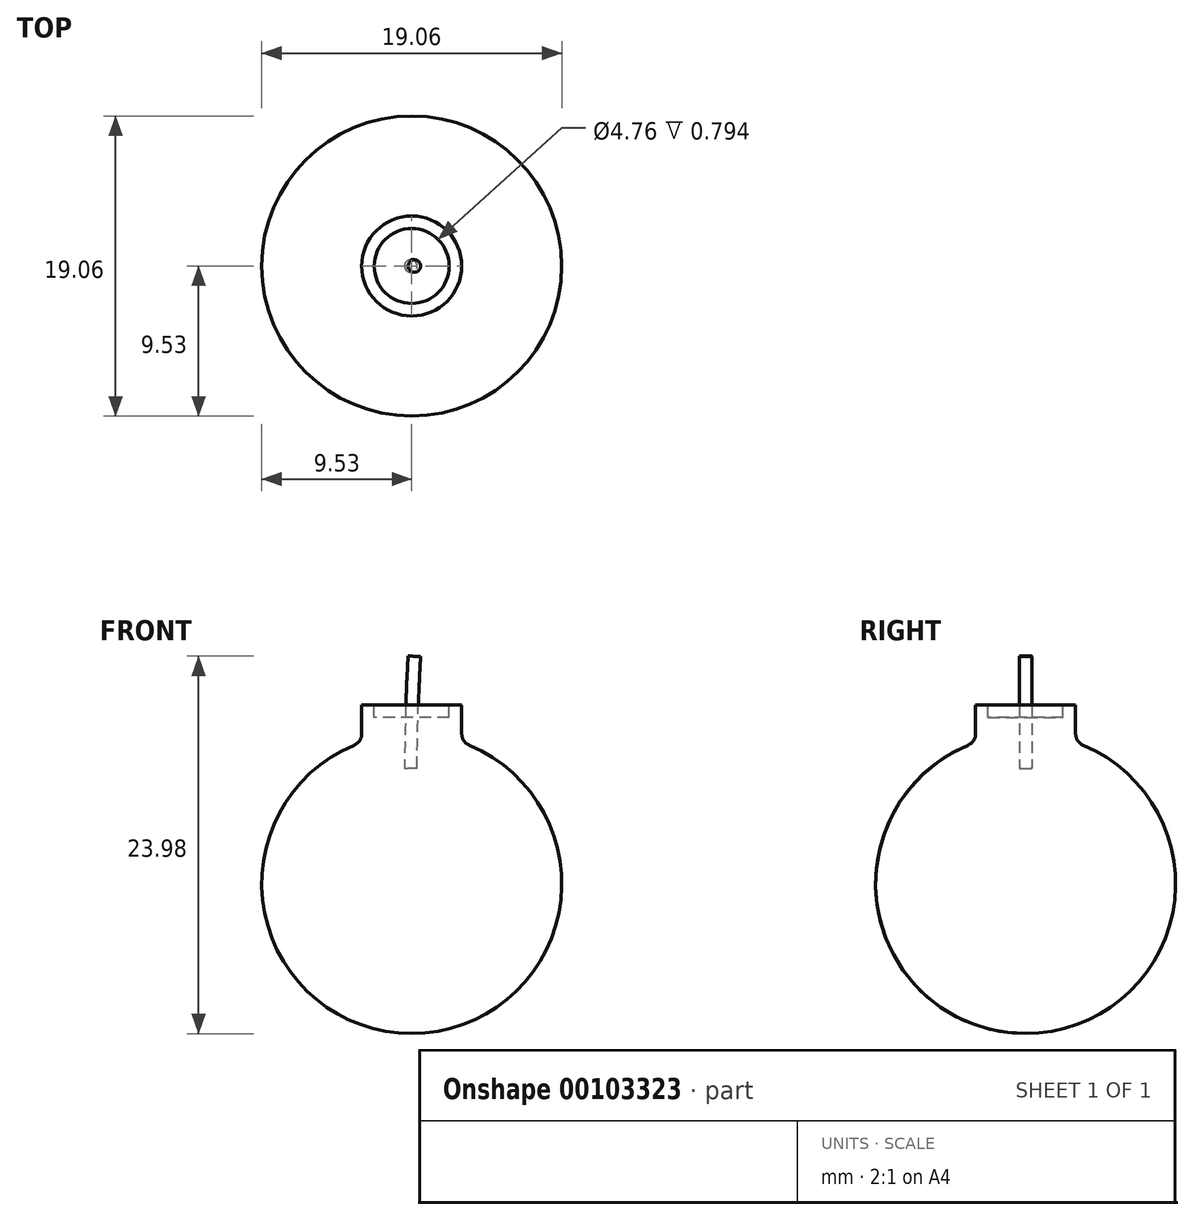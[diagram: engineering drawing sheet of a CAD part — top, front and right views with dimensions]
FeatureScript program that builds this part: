
annotation { "Feature Type Name" : "Feature", "Feature Type Description" : "" }
export const myFeature = defineFeature(function(context is Context, id is Id, definition is map)
    precondition{}
    {
        {
            var Q0;
            Q0=qCreatedBy(makeId("Right.planeOp"),FACE);
            var sketch = newSketch(context, id + "F0", { "sketchPlane" : qUnion([Q0])});
            skArc(sketch, "E0", {"start": v(0, 38.1) * mm, "mid": v(-38.1, 0) * mm, "end": v(0, -38.1) * mm});
            skLineSegment(sketch, "E1", {"start": v(0, 64.9) * mm, "end": v(0, -66.83) * mm});
            skSolve(sketch);
        }
        {
            var Q0;
            {var subQ0=sQuery(id+"F0.wireOp",EDGE,"E0");Q0=makeQuery(id+"F0.imprint","IMPRINT",FACE,{"disambiguationData":[TD([[makeQuery(id+"F0.imprint","IMPRINT",EDGE,{"derivedFrom":subQ0}),1.0]])]});}
            var Q1;
            Q1=sQuery(id+"F0.wireOp",EDGE,"E1");
            revolve(context, id + "F1", {"entities" : qUnion([Q0]), "axis" : qUnion([Q1]), "revolveType" : RevolveType.FULL, "oppositeDirection" : true});
        }
        {
            var Q0;
            Q0=qCreatedBy(makeId("Top.planeOp"),FACE);
            var sketch = newSketch(context, id + "F2", { "sketchPlane" : qUnion([Q0])});
            skCircle(sketch, "E2", {"center": v(0, 0) * mm, "radius": 12.7 * mm});
            skSolve(sketch);
        }
        {
            var Q0;
            Q0=qSketchRegion(id+"F2",true);
            extrude(context, id + "F3", {"entities" : qUnion([Q0]), "operationType" : NewBodyOperationType.ADD, "depth" : 45.35 * mm});
        }
        {
            var Q0;
            Q0=makeQuery(id+"F3.opExtrude","CAP_FACE",FACE,{"disambiguationData":[OSD([sQuery(id+"F2.wireOp",EDGE,"E2")])],"isStart":false});
            var sketch = newSketch(context, id + "F4", { "sketchPlane" : qUnion([Q0])});
            skCircle(sketch, "E3", {"center": v(0, 0) * mm, "radius": 9.53 * mm});
            skSolve(sketch);
        }
        {
            var Q0;
            Q0=qSketchRegion(id+"F4",true);
            extrude(context, id + "F5", {"entities" : qUnion([Q0]), "operationType" : NewBodyOperationType.REMOVE, "oppositeDirection" : true, "depth" : 3.17 * mm});
        }
        {
            var Q0;
            Q0=makeQuery(id+"F3.boolean.opBoolean","INTERSECT",EDGE,{"derivedFrom":[makeQuery(id+"F1.opRevolve","SWEPT_FACE",FACE,{"disambiguationData":[OSD([sQuery(id+"F0.wireOp",EDGE,"E0")])]}),makeQuery(id+"F3.opExtrude","SWEPT_FACE",FACE,{"disambiguationData":[OSD([sQuery(id+"F2.wireOp",EDGE,"E2")])]})]});
            fillet(context, id + "F6", {"entities" : qUnion([Q0]), "radius" : 3.17 * mm, "allowEdgeOverflow" : false});
        }
        {
            var Q0;
            Q0=makeQuery(id+"F5.boolean.opBoolean","COPY",FACE,{"derivedFrom":makeQuery(id+"F5.opExtrude","CAP_FACE",FACE,{"disambiguationData":[OSD([sQuery(id+"F4.wireOp",EDGE,"E3")])],"isStart":false})});
            var sketch = newSketch(context, id + "F7", { "sketchPlane" : qUnion([Q0])});
            skCircle(sketch, "E4", {"center": v(0, 0) * mm, "radius": 1.59 * mm});
            skSolve(sketch);
        }
        {
            var Q0;
            Q0=qCreatedBy(makeId("Front.planeOp"),FACE);
            var sketch = newSketch(context, id + "F8", { "sketchPlane" : qUnion([Q0])});
            skFitSpline(sketch, "E5", {"points": [v(0, 29.24) * mm, v(0.6, 52.42) * mm, v(0.9, 57.77) * mm], "startDerivative": vector(0, 34.16) * mm, "endDerivative": vector(0.6, 11.68) * mm});
            skSolve(sketch);
        }
        {
            var Q0;
            Q0=makeQuery(id+"F7.imprint","IMPRINT",FACE,{"disambiguationData":[TD([[makeQuery(id+"F7.imprint","IMPRINT",EDGE,{"derivedFrom":sQuery(id+"F7.wireOp",EDGE,"E4")}),1.0]])]});
            var Q1;
            Q1=sQuery(id+"F8.wireOp",EDGE,"E5");
            sweep(context, id + "F9", {"profiles" : qUnion([Q0]), "path" : qUnion([Q1])});
        }
        {
            var Q0;
            Q0=makeQuery(id+"F1.opRevolve","SWEPT_BODY",BODY,{"disambiguationData":[OSD([sQuery(id+"F0.wireOp",EDGE,"E0"),sQuery(id+"F0.wireOp",EDGE,"E1")])]});
            var Q1;
            Q1=makeQuery(id+"F9.opSweep","SWEPT_BODY",BODY,{"disambiguationData":[OSD([sQuery(id+"F7.wireOp",EDGE,"E4"),sQuery(id+"F8.wireOp",EDGE,"E5")])]});
            var Q2;
            Q2=qCreatedBy(makeId("Origin.pointOp"),VERTEX);
            transform(context, id + "F10", {"entities" : qUnion([Q0, Q1]), "transformType" : TransformType.SCALE_UNIFORMLY, "scale" : .25, "scalePoint" : qUnion([Q2]), "makeCopy" : false});
        }
    });
